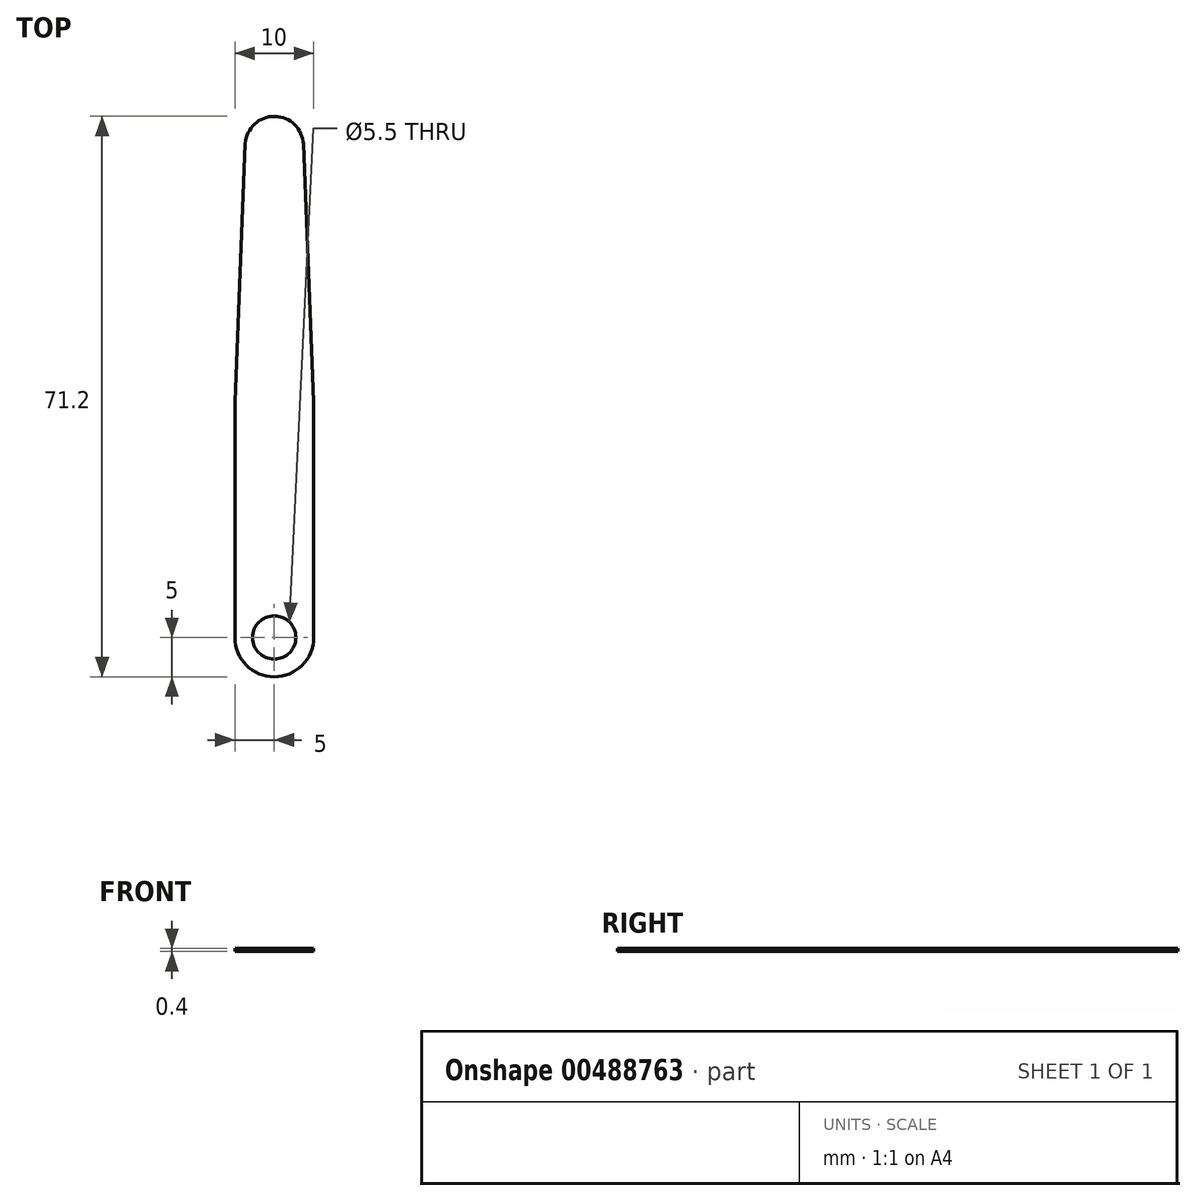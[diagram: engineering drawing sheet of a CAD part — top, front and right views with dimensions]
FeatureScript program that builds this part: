
annotation { "Feature Type Name" : "Feature", "Feature Type Description" : "" }
export const myFeature = defineFeature(function(context is Context, id is Id, definition is map)
    precondition{}
    {
        {
            var Q0;
            Q0=qCreatedBy(makeId("Top.planeOp"),FACE);
            var sketch = newSketch(context, id + "F0", { "sketchPlane" : qUnion([Q0])});
            skArc(sketch, "E0", {"start": v(-5, 0) * mm, "mid": v(0, -5) * mm, "end": v(5, 0) * mm});
            skCircle(sketch, "E1", {"center": v(0, 0) * mm, "radius": 2.75 * mm});
            skLineSegment(sketch, "E2.left", {"start": v(-5, 0) * mm, "end": v(-5, 30) * mm});
            skLineSegment(sketch, "E2.right", {"start": v(5, 0) * mm, "end": v(5, 30) * mm});
            skLineSegment(sketch, "E3", {"start": v(-5, 30) * mm, "end": v(-3.7, 62.74) * mm});
            skLineSegment(sketch, "E4", {"start": v(5, 30) * mm, "end": v(3.7, 62.65) * mm});
            skPoint(sketch, "E5.center.orphan", {"position": v(0, 62.5) * mm});
            skArc(sketch, "E6", {"start": v(3.7, 62.65) * mm, "mid": v(-0.04, 66.2) * mm, "end": v(-3.7, 62.56) * mm});
            skSolve(sketch);
        }
        {
            var Q0;
            Q0=makeQuery(id+"F0.imprint","IMPRINT",FACE,{"disambiguationData":[TD([[makeQuery(id+"F0.imprint","IMPRINT",EDGE,{"derivedFrom":sQuery(id+"F0.wireOp",EDGE,"E0")}),1.0]])]});
            extrude(context, id + "F1", {"entities" : qUnion([Q0]), "depth" : 0.4 * mm, "offsetDistance" : 25 * mm});
        }
    });
